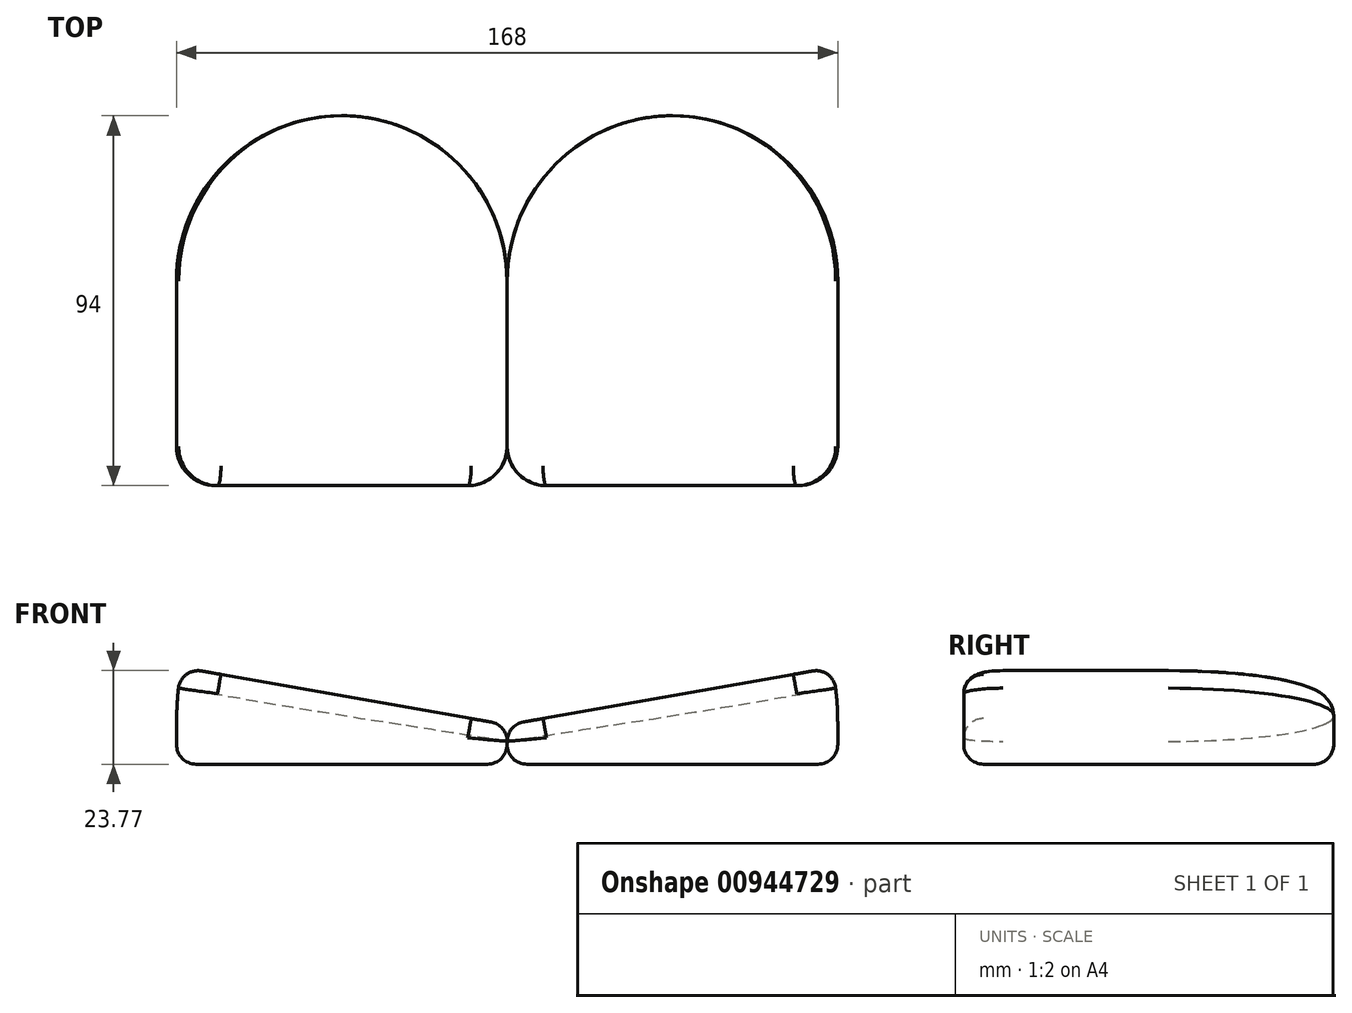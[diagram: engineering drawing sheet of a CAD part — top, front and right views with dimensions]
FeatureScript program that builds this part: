
annotation { "Feature Type Name" : "Feature", "Feature Type Description" : "" }
export const myFeature = defineFeature(function(context is Context, id is Id, definition is map)
    precondition{}
    {
        {
            var Q0;
            Q0=qCreatedBy(makeId("Top.planeOp"),FACE);
            var sketch = newSketch(context, id + "F0", { "sketchPlane" : qUnion([Q0])});
            skCircle(sketch, "E0", {"center": v(0, 0) * mm, "radius": 42 * mm});
            skLineSegment(sketch, "E1.bottom", {"start": v(-42, 0) * mm, "end": v(42, 0) * mm});
            skLineSegment(sketch, "E1.top", {"start": v(-32, -52) * mm, "end": v(32, -52) * mm});
            skLineSegment(sketch, "E1.left", {"start": v(-42, 0) * mm, "end": v(-42, -42) * mm});
            skLineSegment(sketch, "E1.right", {"start": v(42, 0) * mm, "end": v(42, -42) * mm});
            skPoint(sketch, "E2.visualSharp", {"position": v(-42, -52) * mm});
            skArc(sketch, "E2.filletArc", {"start": v(-42, -42) * mm, "mid": v(-39.07, -49.07) * mm, "end": v(-32, -52) * mm});
            skPoint(sketch, "E3.visualSharp", {"position": v(42, -52) * mm});
            skArc(sketch, "E3.filletArc", {"start": v(32, -52) * mm, "mid": v(39.07, -49.07) * mm, "end": v(42, -42) * mm});
            skSolve(sketch);
        }
        {
            var Q0;
            {var subQ0=sQuery(id+"F0.wireOp",EDGE,"E1.bottom");Q0=makeQuery(id+"F0.imprint","IMPRINT",FACE,{"disambiguationData":[TD([[makeQuery(id+"F0.imprint","IMPRINT",EDGE,{"derivedFrom":subQ0}),1.0]])]});}
            var Q1;
            {var subQ0=sQuery(id+"F0.wireOp",EDGE,"E1.bottom");Q1=makeQuery(id+"F0.imprint","IMPRINT",FACE,{"disambiguationData":[TD([[makeQuery(id+"F0.imprint","IMPRINT",EDGE,{"derivedFrom":subQ0}),-1.0]])]});}
            var Q2;
            Q2=makeQuery(id+"F0.imprint","IMPRINT",FACE,{"disambiguationData":[TD([[makeQuery(id+"F0.imprint","IMPRINT",EDGE,{"derivedFrom":sQuery(id+"F0.wireOp",EDGE,"E1.top")}),1.0]])]});
            extrude(context, id + "F1", {"entities" : qUnion([Q0, Q1, Q2]), "depth" : 10 * mm, "offsetDistance" : 25.4 * mm});
        }
        {
            var Q0;
            Q0=makeQuery(id+"F1.opExtrude","CAP_FACE",FACE,{"disambiguationData":[OSD([sQuery(id+"F0.wireOp",EDGE,"E0"),sQuery(id+"F0.wireOp",EDGE,"E1.top"),sQuery(id+"F0.wireOp",EDGE,"E1.left"),sQuery(id+"F0.wireOp",EDGE,"E1.right"),sQuery(id+"F0.wireOp",EDGE,"E2.filletArc"),sQuery(id+"F0.wireOp",EDGE,"E3.filletArc")])],"isStart":false});
            var Q1;
            Q1=makeQuery(id+"F1.opExtrude","CAP_EDGE",EDGE,{"disambiguationData":[OSD([sQuery(id+"F0.wireOp",EDGE,"E1.left")])],"isStart":false});
            revolve(context, id + "F2", {"operationType" : NewBodyOperationType.ADD, "surfaceOperationType" : NewSurfaceOperationType.NEW, "entities" : qUnion([Q0]), "axis" : qUnion([Q1]), "revolveType" : RevolveType.ONE_DIRECTION, "angle" : 10 * degree});
        }
        {
            var Q0;
            Q0=makeQuery(id+"F2.opRevolve","CAP_EDGE",EDGE,{"disambiguationData":[OSD([sQuery(id+"F0.wireOp",EDGE,"E0")])],"isStart":false});
            var Q1;
            Q1=makeQuery(id+"F1.opExtrude","SWEPT_FACE",FACE,{"disambiguationData":[OSD([sQuery(id+"F0.wireOp",EDGE,"E0")])]});
            var Q2;
            Q2=makeQuery(id+"F2.opRevolve","SWEPT_FACE",FACE,{"disambiguationData":[OSD([sQuery(id+"F0.wireOp",EDGE,"E3.filletArc")])]});
            var Q3;
            Q3=makeQuery(id+"F1.opExtrude","CAP_FACE",FACE,{"disambiguationData":[OSD([sQuery(id+"F0.wireOp",EDGE,"E0"),sQuery(id+"F0.wireOp",EDGE,"E1.top"),sQuery(id+"F0.wireOp",EDGE,"E1.left"),sQuery(id+"F0.wireOp",EDGE,"E1.right"),sQuery(id+"F0.wireOp",EDGE,"E2.filletArc"),sQuery(id+"F0.wireOp",EDGE,"E3.filletArc")])],"isStart":true});
            var Q4;
            Q4=makeQuery(id+"F2.opRevolve","SWEPT_FACE",FACE,{"disambiguationData":[OSD([sQuery(id+"F0.wireOp",EDGE,"E2.filletArc")])]});
            var Q5;
            Q5=makeQuery(id+"F1.opExtrude","SWEPT_FACE",FACE,{"disambiguationData":[OSD([sQuery(id+"F0.wireOp",EDGE,"E1.left")])]});
            var Q6;
            Q6=makeQuery(id+"F2.opRevolve","SWEPT_FACE",FACE,{"disambiguationData":[OSD([sQuery(id+"F0.wireOp",EDGE,"E1.right")])]});
            var Q7;
            Q7=makeQuery(id+"F1.opExtrude","SWEPT_FACE",FACE,{"disambiguationData":[OSD([sQuery(id+"F0.wireOp",EDGE,"E1.right")])]});
            var Q8;
            Q8=makeQuery(id+"F1.opExtrude","SWEPT_FACE",FACE,{"disambiguationData":[OSD([sQuery(id+"F0.wireOp",EDGE,"E2.filletArc")])]});
            var Q9;
            Q9=makeQuery(id+"F1.opExtrude","SWEPT_FACE",FACE,{"disambiguationData":[OSD([sQuery(id+"F0.wireOp",EDGE,"E3.filletArc")])]});
            var Q10;
            Q10=makeQuery(id+"F2.opRevolve","SWEPT_FACE",FACE,{"disambiguationData":[OSD([sQuery(id+"F0.wireOp",EDGE,"E0")])]});
            var Q11;
            Q11=makeQuery(id+"F1.opExtrude","CAP_EDGE",EDGE,{"disambiguationData":[OSD([sQuery(id+"F0.wireOp",EDGE,"E1.right")])],"isStart":true});
            var Q12;
            Q12=makeQuery(id+"F2.opRevolve","CAP_FACE",FACE,{"disambiguationData":[OSD([sQuery(id+"F0.wireOp",EDGE,"E0"),sQuery(id+"F0.wireOp",EDGE,"E1.top"),sQuery(id+"F0.wireOp",EDGE,"E1.left"),sQuery(id+"F0.wireOp",EDGE,"E1.right"),sQuery(id+"F0.wireOp",EDGE,"E2.filletArc"),sQuery(id+"F0.wireOp",EDGE,"E3.filletArc")])],"isStart":false});
            var Q13;
            Q13=makeQuery(id+"F2.opRevolve","CAP_EDGE",EDGE,{"disambiguationData":[OSD([sQuery(id+"F0.wireOp",EDGE,"E1.right")])],"isStart":false});
            var Q14;
            {var subQ0=sQuery(id+"F0.wireOp",EDGE,"E1.top");Q14=makeQuery(id+"F2.boolean.opBoolean","MERGE",FACE,{"derivedFrom":[makeQuery(id+"F1.opExtrude","SWEPT_FACE",FACE,{"disambiguationData":[OSD([subQ0])]}),makeQuery(id+"F2.opRevolve","SWEPT_FACE",FACE,{"disambiguationData":[OSD([subQ0])]})]});}
            var Q15;
            {var subQ0=sQuery(id+"F0.wireOp",EDGE,"E1.left");Q15=makeQuery(id+"F2.boolean.opBoolean","MERGE",EDGE,{"derivedFrom":[makeQuery(id+"F1.opExtrude","CAP_EDGE",EDGE,{"disambiguationData":[OSD([subQ0])],"isStart":false}),makeQuery(id+"F2.opRevolve","CAP_EDGE",EDGE,{"disambiguationData":[OSD([subQ0])],"isStart":true})]});}
            var Q16;
            {var subQ0=sQuery(id+"F0.wireOp",EDGE,"E1.right");Q16=makeQuery(id+"F2.boolean.opBoolean","MERGE",EDGE,{"derivedFrom":[makeQuery(id+"F1.opExtrude","CAP_EDGE",EDGE,{"disambiguationData":[OSD([subQ0])],"isStart":false}),makeQuery(id+"F2.opRevolve","CAP_EDGE",EDGE,{"disambiguationData":[OSD([subQ0])],"isStart":true})]});}
            var Q17;
            Q17=makeQuery(id+"F1.opExtrude","CAP_EDGE",EDGE,{"disambiguationData":[OSD([sQuery(id+"F0.wireOp",EDGE,"E2.filletArc")])],"isStart":true});
            var Q18;
            Q18=makeQuery(id+"F1.opExtrude","SWEPT_EDGE",EDGE,{"disambiguationData":[OSD([sQuery(id+"F0.wireOp",EDGE,"E0"),sQuery(id+"F0.wireOp",EDGE,"E1.bottom"),sQuery(id+"F0.wireOp",EDGE,"E1.left")])]});
            var Q19;
            Q19=makeQuery(id+"F1.opExtrude","SWEPT_EDGE",EDGE,{"disambiguationData":[OSD([sQuery(id+"F0.wireOp",EDGE,"E0"),sQuery(id+"F0.wireOp",EDGE,"E1.bottom"),sQuery(id+"F0.wireOp",EDGE,"E1.right")])]});
            var Q20;
            Q20=makeQuery(id+"F1.opExtrude","SWEPT_EDGE",EDGE,{"disambiguationData":[OSD([sQuery(id+"F0.wireOp",EDGE,"E1.top"),sQuery(id+"F0.wireOp",EDGE,"E2.filletArc")])]});
            var Q21;
            Q21=makeQuery(id+"F1.opExtrude","SWEPT_EDGE",EDGE,{"disambiguationData":[OSD([sQuery(id+"F0.wireOp",EDGE,"E1.top"),sQuery(id+"F0.wireOp",EDGE,"E3.filletArc")])]});
            var Q22;
            Q22=makeQuery(id+"F2.opRevolve","SWEPT_EDGE",EDGE,{"disambiguationData":[OSD([sQuery(id+"F0.wireOp",EDGE,"E1.right"),sQuery(id+"F0.wireOp",EDGE,"E3.filletArc")])]});
            var Q23;
            Q23=makeQuery(id+"F1.opExtrude","SWEPT_EDGE",EDGE,{"disambiguationData":[OSD([sQuery(id+"F0.wireOp",EDGE,"E1.left"),sQuery(id+"F0.wireOp",EDGE,"E2.filletArc")])]});
            var Q24;
            Q24=makeQuery(id+"F1.opExtrude","SWEPT_EDGE",EDGE,{"disambiguationData":[OSD([sQuery(id+"F0.wireOp",EDGE,"E1.right"),sQuery(id+"F0.wireOp",EDGE,"E3.filletArc")])]});
            var Q25;
            Q25=makeQuery(id+"F1.opExtrude","CAP_EDGE",EDGE,{"disambiguationData":[OSD([sQuery(id+"F0.wireOp",EDGE,"E0")])],"isStart":true});
            var Q26;
            Q26=makeQuery(id+"F2.opRevolve","SWEPT_EDGE",EDGE,{"disambiguationData":[OSD([sQuery(id+"F0.wireOp",EDGE,"E1.top"),sQuery(id+"F0.wireOp",EDGE,"E3.filletArc")])]});
            var Q27;
            Q27=makeQuery(id+"F1.opExtrude","CAP_EDGE",EDGE,{"disambiguationData":[OSD([sQuery(id+"F0.wireOp",EDGE,"E1.top")])],"isStart":true});
            var Q28;
            Q28=makeQuery(id+"F1.opExtrude","CAP_EDGE",EDGE,{"disambiguationData":[OSD([sQuery(id+"F0.wireOp",EDGE,"E1.left")])],"isStart":true});
            var Q29;
            Q29=makeQuery(id+"F2.opRevolve","SWEPT_EDGE",EDGE,{"disambiguationData":[OSD([sQuery(id+"F0.wireOp",EDGE,"E0"),sQuery(id+"F0.wireOp",EDGE,"E1.bottom"),sQuery(id+"F0.wireOp",EDGE,"E1.right")])]});
            var Q30;
            Q30=makeQuery(id+"F2.opRevolve","CAP_EDGE",EDGE,{"disambiguationData":[OSD([sQuery(id+"F0.wireOp",EDGE,"E3.filletArc")])],"isStart":false});
            var Q31;
            Q31=makeQuery(id+"F1.opExtrude","CAP_EDGE",EDGE,{"disambiguationData":[OSD([sQuery(id+"F0.wireOp",EDGE,"E3.filletArc")])],"isStart":true});
            var Q32;
            Q32=makeQuery(id+"F2.opRevolve","CAP_EDGE",EDGE,{"disambiguationData":[OSD([sQuery(id+"F0.wireOp",EDGE,"E1.top")])],"isStart":false});
            var Q33;
            Q33=makeQuery(id+"F2.opRevolve","CAP_EDGE",EDGE,{"disambiguationData":[OSD([sQuery(id+"F0.wireOp",EDGE,"E2.filletArc")])],"isStart":false});
            var Q34;
            {var subQ0=sQuery(id+"F0.wireOp",EDGE,"E0");Q34=makeQuery(id+"F2.boolean.opBoolean","MERGE",EDGE,{"derivedFrom":[makeQuery(id+"F1.opExtrude","CAP_EDGE",EDGE,{"disambiguationData":[OSD([subQ0])],"isStart":false}),makeQuery(id+"F2.opRevolve","CAP_EDGE",EDGE,{"disambiguationData":[OSD([subQ0])],"isStart":true})]});}
            var Q35;
            {var subQ0=sQuery(id+"F0.wireOp",EDGE,"E2.filletArc");Q35=makeQuery(id+"F2.boolean.opBoolean","MERGE",EDGE,{"derivedFrom":[makeQuery(id+"F1.opExtrude","CAP_EDGE",EDGE,{"disambiguationData":[OSD([subQ0])],"isStart":false}),makeQuery(id+"F2.opRevolve","CAP_EDGE",EDGE,{"disambiguationData":[OSD([subQ0])],"isStart":true})]});}
            var Q36;
            {var subQ0=sQuery(id+"F0.wireOp",EDGE,"E3.filletArc");Q36=makeQuery(id+"F2.boolean.opBoolean","MERGE",EDGE,{"derivedFrom":[makeQuery(id+"F1.opExtrude","CAP_EDGE",EDGE,{"disambiguationData":[OSD([subQ0])],"isStart":false}),makeQuery(id+"F2.opRevolve","CAP_EDGE",EDGE,{"disambiguationData":[OSD([subQ0])],"isStart":true})]});}
            var Q37;
            Q37=makeQuery(id+"F2.opRevolve","SWEPT_EDGE",EDGE,{"disambiguationData":[OSD([sQuery(id+"F0.wireOp",EDGE,"E1.top"),sQuery(id+"F0.wireOp",EDGE,"E2.filletArc")])]});
            fillet(context, id + "F3", {"entities" : qUnion([Q0, Q1, Q2, Q3, Q4, Q5, Q6, Q7, Q8, Q9, Q10, Q11, Q12, Q13, Q14, Q15, Q16, Q17, Q18, Q19, Q20, Q21, Q22, Q23, Q24, Q25, Q26, Q27, Q28, Q29, Q30, Q31, Q32, Q33, Q34, Q35, Q36, Q37]), "radius" : 5 * mm, "tangentPropagation" : true, "allowEdgeOverflow" : false});
        }
        {
            var Q0;
            Q0=makeQuery(id+"F1.opExtrude","SWEPT_BODY",BODY,{"disambiguationData":[OSD([sQuery(id+"F0.wireOp",EDGE,"E0"),sQuery(id+"F0.wireOp",EDGE,"E1.top"),sQuery(id+"F0.wireOp",EDGE,"E1.left"),sQuery(id+"F0.wireOp",EDGE,"E1.right"),sQuery(id+"F0.wireOp",EDGE,"E2.filletArc"),sQuery(id+"F0.wireOp",EDGE,"E3.filletArc")])]});
            var Q1;
            Q1=makeQuery(id+"F1.opExtrude","SWEPT_FACE",FACE,{"disambiguationData":[OSD([sQuery(id+"F0.wireOp",EDGE,"E1.left")])]});
            mirror(context, id + "F4", {"entities" : qUnion([Q0]), "mirrorPlane" : qUnion([Q1])});
        }
    });
